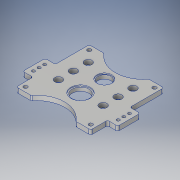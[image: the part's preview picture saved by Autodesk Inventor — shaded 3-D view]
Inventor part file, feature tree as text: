
AUTODESK INVENTOR PART (.ipt)
format: ipt  version: 2019 (Build 230136000, 136)  size: 290,816 bytes
history: native  units: in
note: dims shown in document units (in); Inventor stores cm internally (conversion verified against a paired STEP export)
features: extrude x6, sketch x6, fillet x3
ambient origin geometry x8: Origin, YZ Plane, XZ Plane, XY Plane, X Axis, Y Axis, Z Axis, Center Point
bodies: Solid1 (feature_tree)
feature tree (15):
  extrude  "Extrusion1"  Depth=4.9in
  extrude  "Extrusion2"  Depth=0.3125in
  fillet  "Fillet1"  Radius=0.312in
  extrude  "Extrusion6"  Depth=0.312in
  extrude  "Extrusion7"  Depth=0.256in
  fillet  "Fillet3"  Radius=1.0in
  extrude  "Extrusion8"  Depth=0.5in
  fillet  "Fillet4"  Radius=0.5in
  extrude  "Extrusion9"  Depth=1.125in
  sketch  "Sketch1"  dims[d0=5.0in d1=4.9in]
  sketch  "Sketch2"  dims[d2=0.3125in d3=0.0in d4=0.312in d5=0.312in]
  sketch  "Sketch6"  dims[d6=0.312in d7=0.312in]
  sketch  "Sketch7"  dims[d8=0.256in d9=0.256in d10=1.0in]
  sketch  "Sketch8"  dims[d11=1.067in d12=1.0in d14=0.5in]
  sketch  "Sketch12"  dims[d15=1.0in d17=1.125in d18=1.602in d19=0.3125in d20=0.0in d21=0.125in d47=0.125in d48=1.5in d49=0.688in d50=0.688in d51=0.3125in d52=0.0in d53=0.375in d54=0.375in d55=0.2in d56=0.344in d57=0.3125in d58=0.0in d59=0.125in d60=0.75in d61=1.5in d62=3.0in d63=0.75in d64=0.3125in d65=0.0in d66=1.067in d67=0.125in d69=1.5in d70=0.375in d71=0.375in d72=0.375in d75=1.0in d76=1.485in d77=1.5in d78=1.5in d79=0.125in d80=1.0in d81=1.0in d82=1.125in d83=1.125in d84=1.0in d97=1.3in d98=1.0in d99=0.0625in d100=0.0in]
